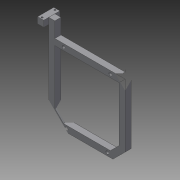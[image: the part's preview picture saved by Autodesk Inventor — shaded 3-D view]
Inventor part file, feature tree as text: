
AUTODESK INVENTOR PART (.ipt)
format: ipt  version: 2014 SP1 (Build 180222100, 222)  size: 152,576 bytes
history: native  units: in
note: dims shown in document units (in); Inventor stores cm internally (conversion verified against a paired STEP export)
features: extrude x3, mirror x2, sketch x2
ambient origin geometry x8: Origin, YZ Plane, XZ Plane, XY Plane, X Axis, Y Axis, Z Axis, Center Point
bodies: Solid1 (feature_tree)
feature tree (7):
  extrude  "Extrusion1"  Depth=5.67in
  extrude  "Extrusion4"  Depth=0.5in
  mirror  "Mirror1"
  extrude  "Extrusion5"  Depth=0.5in
  mirror  "Mirror2"
  sketch  "Sketch4"  dims[d1=5.67in d2=0.25in]
  sketch  "Sketch6"  dims[d3=0.25in d4=0.5in d5=0.5in d8=0.5in d9=0.0in d15=0.5in d16=0.5in d17=0.5in d18=0.0in d20=1.0in d21=0.0in d22=0.25in d23=0.25in d24=0.25in d25=0.25in d26=0.25in d27=0.25in d28=0.5in d29=0.0in d30=0.5305in d31=1.061in]
